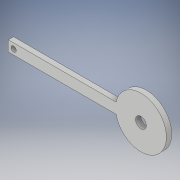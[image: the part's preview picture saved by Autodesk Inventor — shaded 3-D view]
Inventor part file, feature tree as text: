
AUTODESK INVENTOR PART (.ipt)
format: ipt  version: 2017 (Build 210142000, 142)  size: 129,536 bytes
history: native  units: in
note: dims shown in document units (in); Inventor stores cm internally (conversion verified against a paired STEP export)
features: sketch x5, extrude x4, hole x2, plane x1
ambient origin geometry x8: Origin, YZ Plane, XZ Plane, XY Plane, X Axis, Y Axis, Z Axis, Center Point
bodies: Solid1 (feature_tree)
feature tree (12):
  extrude  "Extrusion1"  Depth=0.125in
  sketch  "Sketch2"  dims[d1=0.125in d2=0.0in d3=0.125in]
  plane  "Work Plane1"
  extrude  "Extrusion2"  Depth=0.25in
  extrude  "Extrusion3"  Depth=0.5in TaperAngle=0.0deg
  sketch  "Sketch6"  dims[d24=0.255in]
  hole  "Hole1"  [1 undecoded]
  hole  "Hole2"  [1 undecoded]
  extrude  "Extrusion6"  Depth=0.125in TaperAngle=0.0deg
  sketch  "Sketch3"  dims[d4=0.125in d6=0.25in]
  sketch  "Sketch4"  dims[d7=2.5295in d8=0.0in d9=0.5in d10=0.0in]
  sketch  "Sketch7"  dims[d25=0.255in d26=0.75in d27=0.375in d28=0.25in d29=0.5635in d30=1.0in d31=0.8108in d32=0.255in d33=0.75in d34=0.375in d35=0.25in d36=0.5635in d37=0.3125in d38=0.8108in d39=0.125in d40=0.125in d41=1.0in d42=0.0in]
note: 2 required parameter values undecoded (feature->parameter linkage not recoverable at this tier; creation-order binding heuristic only, values carry confidence <= 0.55)
